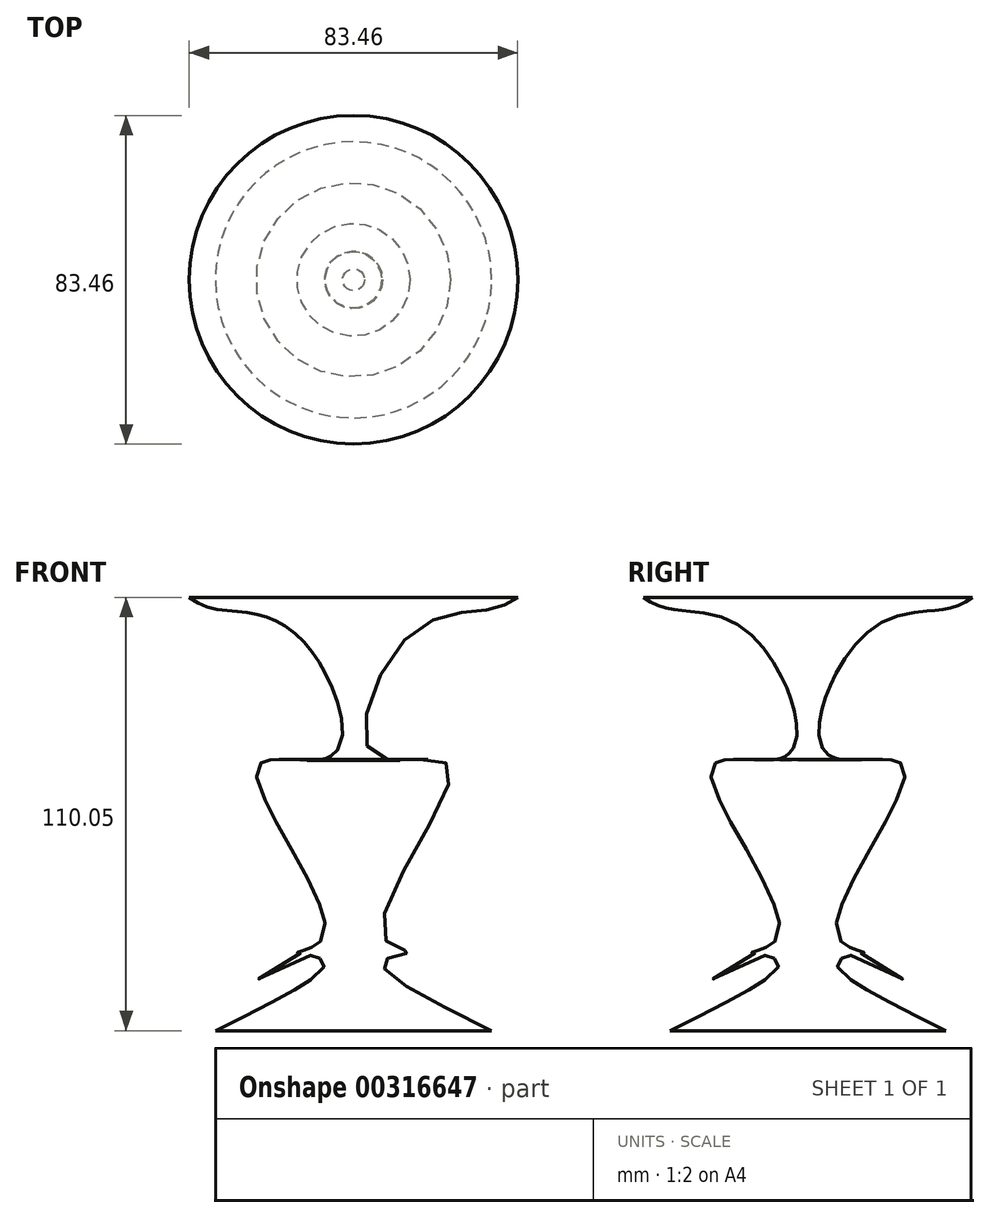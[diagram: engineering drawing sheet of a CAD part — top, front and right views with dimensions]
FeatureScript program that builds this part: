
annotation { "Feature Type Name" : "Feature", "Feature Type Description" : "" }
export const myFeature = defineFeature(function(context is Context, id is Id, definition is map)
    precondition{}
    {
        {
            var Q0;
            Q0=qCreatedBy(makeId("Front.planeOp"),FACE);
            var sketch = newSketch(context, id + "F0", { "sketchPlane" : qUnion([Q0])});
            skLineSegment(sketch, "E0", {"start": v(0, 68.58) * mm, "end": v(0, -59.8) * mm, "construction": true});
            skLineSegment(sketch, "E1", {"start": v(0, -59.8) * mm, "end": v(-35.09, -59.8) * mm});
            skFitSpline(sketch, "E2", {"points": [v(-35.09, -59.8) * mm, v(-7.7, -42) * mm, v(-14.35, -39.87) * mm, v(-7.44, -35.62) * mm, v(-24.45, 7.18) * mm, v(-5.05, 10.37) * mm, v(-14.89, 41.2) * mm, v(-35.09, 47.31) * mm, v(-41.73, 50.24) * mm], "startDerivative": vector(281.35, 137.94) * mm, "endDerivative": vector(-73.2, 46.94) * mm});
            skLineSegment(sketch, "E3", {"start": v(-41.73, 50.24) * mm, "end": v(0, 50.24) * mm});
            skLineSegment(sketch, "E4", {"start": v(0, 50.24) * mm, "end": v(0, -59.8) * mm});
            skSolve(sketch);
        }
        {
            var Q0;
            Q0=makeQuery(id+"F0.imprint","IMPRINT",FACE,{"disambiguationData":[TD([[makeQuery(id+"F0.imprint","IMPRINT",EDGE,{"derivedFrom":sQuery(id+"F0.wireOp",EDGE,"E1")}),-1.0]])]});
            var Q1;
            Q1=sQuery(id+"F0.wireOp",EDGE,"E4");
            revolve(context, id + "F1", {"entities" : qUnion([Q0]), "axis" : qUnion([Q1]), "revolveType" : RevolveType.FULL});
        }
    });
